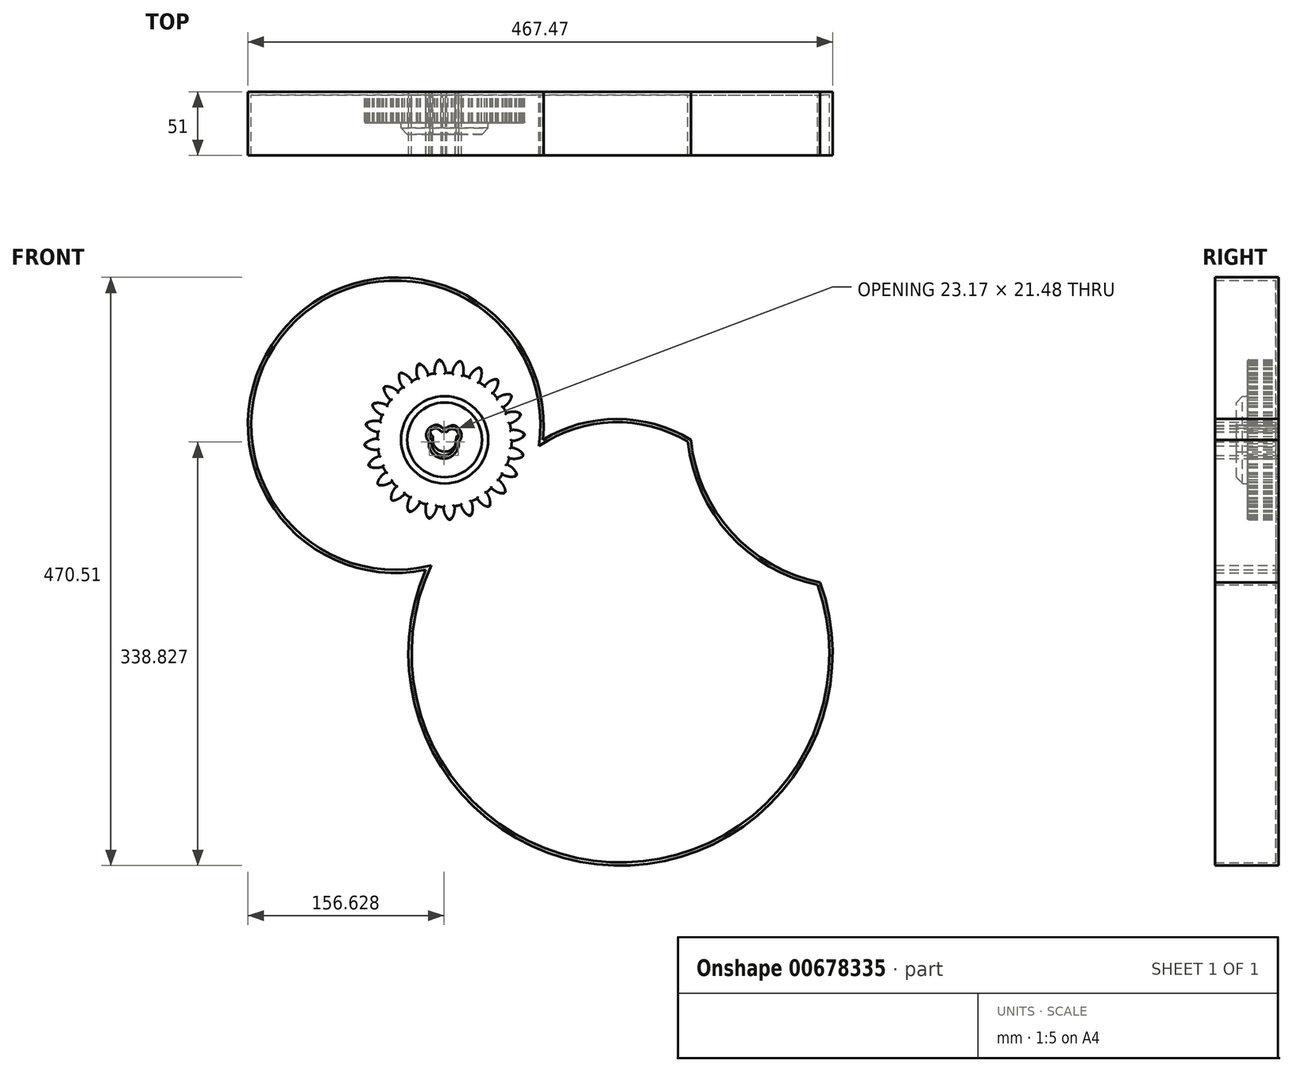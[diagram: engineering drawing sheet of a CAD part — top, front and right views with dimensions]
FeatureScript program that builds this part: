
annotation { "Feature Type Name" : "Feature", "Feature Type Description" : "" }
export const myFeature = defineFeature(function(context is Context, id is Id, definition is map)
    precondition{}
    {
        {
            var Q0;
            Q0=qCreatedBy(makeId("Front.planeOp"),FACE);
            var sketch = newSketch(context, id + "F0", { "sketchPlane" : qUnion([Q0])});
            skCircle(sketch, "E0", {"center": v(0, 0) * mm, "radius": 53.72 * mm});
            skCircle(sketch, "E1", {"center": v(0, 0) * mm, "radius": 58.67 * mm, "construction": true});
            skCircle(sketch, "E2", {"center": v(0, 0) * mm, "radius": 63.5 * mm, "construction": true});
            skLineSegment(sketch, "E3", {"start": v(0, 83.52) * mm, "end": v(0, 0) * mm, "construction": true});
            skLineSegment(sketch, "E4", {"start": v(0, 0) * mm, "end": v(-5.47, 83.52) * mm, "construction": true});
            skLineSegment(sketch, "E5", {"start": v(0, 58.67) * mm, "end": v(-56.46, 38.13) * mm, "construction": true});
            skLineSegment(sketch, "E6", {"start": v(0, 58.67) * mm, "end": v(-59.14, 58.67) * mm, "construction": true});
            skCircle(sketch, "E7", {"center": v(0, 0) * mm, "radius": 55.14 * mm, "construction": true});
            skCircle(sketch, "E8", {"center": v(0, 58.67) * mm, "radius": 14.6 * mm, "construction": true});
            skCircle(sketch, "E9", {"center": v(-13.72, 53.68) * mm, "radius": 14.6 * mm, "construction": true});
            skArc(sketch, "E10", {"start": v(0, 58.67) * mm, "mid": v(-1.18, 61.2) * mm, "end": v(-2.86, 63.44) * mm});
            skArc(sketch, "E11", {"start": v(0.88, 53.71) * mm, "mid": v(0.63, 56.23) * mm, "end": v(0, 58.67) * mm});
            skArc(sketch, "E12.MirrorCS", {"start": v(-7.66, 58.17) * mm, "mid": v(-6.82, 60.84) * mm, "end": v(-5.45, 63.27) * mm});
            skArc(sketch, "E13.MirrorCS", {"start": v(-7.88, 53.14) * mm, "mid": v(-7.97, 55.66) * mm, "end": v(-7.66, 58.17) * mm});
            skArc(sketch, "E14", {"start": v(-2.86, 63.44) * mm, "mid": v(-4.19, 63.92) * mm, "end": v(-5.45, 63.27) * mm});
            skCircle(sketch, "E15", {"center": v(0.01, 0) * mm, "radius": 34.89 * mm});
            skCircle(sketch, "E16", {"center": v(0.01, 0) * mm, "radius": 9.5 * mm});
            skCircle(sketch, "E17", {"center": v(-6.45, 6.97) * mm, "radius": 5.08 * mm});
            skCircle(sketch, "E18", {"center": v(6.77, 6.7) * mm, "radius": 4.94 * mm});
            skSolve(sketch);
        }
        {
            var Q0;
            Q0=makeQuery(id+"F0.imprint","IMPRINT",FACE,{"disambiguationData":[TD([[makeQuery(id+"F0.imprint","IMPRINT",EDGE,{"derivedFrom":sQuery(id+"F0.wireOp",EDGE,"E15")}),-1.0]])]});
            var Q1;
            Q1=makeQuery(id+"F0.imprint","IMPRINT",FACE,{"disambiguationData":[TD([[makeQuery(id+"F0.imprint","IMPRINT",EDGE,{"derivedFrom":sQuery(id+"F0.wireOp",EDGE,"E10")}),1.0]])]});
            extrude(context, id + "F1", {"entities" : qUnion([Q0, Q1]), "depth" : 25 * mm, "offsetDistance" : 25 * mm});
        }
        {
            var Q0;
            Q0=makeQuery(id+"F1.opExtrude","SWEPT_BODY",BODY,{"disambiguationData":[OSD([sQuery(id+"F0.wireOp",EDGE,"E0"),sQuery(id+"F0.wireOp",EDGE,"E10"),sQuery(id+"F0.wireOp",EDGE,"E11"),sQuery(id+"F0.wireOp",EDGE,"E12.MirrorCS"),sQuery(id+"F0.wireOp",EDGE,"E13.MirrorCS"),sQuery(id+"F0.wireOp",EDGE,"E14")])]});
            var Q1;
            Q1=makeQuery(id+"F1.opExtrude","SWEPT_FACE",FACE,{"disambiguationData":[OSD([sQuery(id+"F0.wireOp",EDGE,"E0")])]});
            circularPattern(context, id + "F2", {"entities" : qUnion([Q0]), "axis" : qUnion([Q1]), "angle" : 360 * degree, "instanceCount" : 24, "equalSpace" : true});
        }
        {
            var Q0;
            Q0=makeQuery(id+"F0.imprint","IMPRINT",FACE,{"disambiguationData":[TD([[makeQuery(id+"F0.imprint","IMPRINT",EDGE,{"derivedFrom":sQuery(id+"F0.wireOp",EDGE,"E15")}),1.0]])]});
            extrude(context, id + "F3", {"entities" : qUnion([Q0]), "operationType" : NewBodyOperationType.ADD, "depth" : 33.9 * mm, "offsetDistance" : 25 * mm});
        }
        {
            var Q0;
            Q0=makeQuery(id+"F3.opExtrude","CAP_EDGE",EDGE,{"disambiguationData":[OSD([sQuery(id+"F0.wireOp",EDGE,"E15")])],"isStart":true});
            var Q1;
            Q1=makeQuery(id+"F3.opExtrude","CAP_EDGE",EDGE,{"disambiguationData":[OSD([sQuery(id+"F0.wireOp",EDGE,"E15")])],"isStart":false});
            chamfer(context, id + "F4", {"entities" : qUnion([Q0, Q1]), "width" : 5 * mm, "tangentPropagation" : true});
        }
        {
            var Q0;
            {var subQ0=makeQuery(id+"F1.opExtrude","CAP_FACE",FACE,{"disambiguationData":[OSD([sQuery(id+"F0.wireOp",EDGE,"E0"),sQuery(id+"F0.wireOp",EDGE,"E10"),sQuery(id+"F0.wireOp",EDGE,"E11"),sQuery(id+"F0.wireOp",EDGE,"E12.MirrorCS"),sQuery(id+"F0.wireOp",EDGE,"E13.MirrorCS"),sQuery(id+"F0.wireOp",EDGE,"E14"),sQuery(id+"F0.wireOp",EDGE,"E15")])],"isStart":false});Q0=makeQuery(id+"F3.boolean.opBoolean","MERGE",FACE,{"derivedFrom":[subQ0,makeQuery(id+"F2.opPattern","COPY",FACE,{"derivedFrom":subQ0,"instanceName":"1"}),makeQuery(id+"F2.opPattern","COPY",FACE,{"derivedFrom":subQ0,"instanceName":"2"}),makeQuery(id+"F2.opPattern","COPY",FACE,{"derivedFrom":subQ0,"instanceName":"3"}),makeQuery(id+"F2.opPattern","COPY",FACE,{"derivedFrom":subQ0,"instanceName":"4"}),makeQuery(id+"F2.opPattern","COPY",FACE,{"derivedFrom":subQ0,"instanceName":"5"}),makeQuery(id+"F2.opPattern","COPY",FACE,{"derivedFrom":subQ0,"instanceName":"6"}),makeQuery(id+"F2.opPattern","COPY",FACE,{"derivedFrom":subQ0,"instanceName":"7"}),makeQuery(id+"F2.opPattern","COPY",FACE,{"derivedFrom":subQ0,"instanceName":"8"}),makeQuery(id+"F2.opPattern","COPY",FACE,{"derivedFrom":subQ0,"instanceName":"9"}),makeQuery(id+"F2.opPattern","COPY",FACE,{"derivedFrom":subQ0,"instanceName":"10"}),makeQuery(id+"F2.opPattern","COPY",FACE,{"derivedFrom":subQ0,"instanceName":"11"}),makeQuery(id+"F2.opPattern","COPY",FACE,{"derivedFrom":subQ0,"instanceName":"12"}),makeQuery(id+"F2.opPattern","COPY",FACE,{"derivedFrom":subQ0,"instanceName":"13"}),makeQuery(id+"F2.opPattern","COPY",FACE,{"derivedFrom":subQ0,"instanceName":"14"}),makeQuery(id+"F2.opPattern","COPY",FACE,{"derivedFrom":subQ0,"instanceName":"15"}),makeQuery(id+"F2.opPattern","COPY",FACE,{"derivedFrom":subQ0,"instanceName":"16"}),makeQuery(id+"F2.opPattern","COPY",FACE,{"derivedFrom":subQ0,"instanceName":"17"}),makeQuery(id+"F2.opPattern","COPY",FACE,{"derivedFrom":subQ0,"instanceName":"18"}),makeQuery(id+"F2.opPattern","COPY",FACE,{"derivedFrom":subQ0,"instanceName":"19"}),makeQuery(id+"F2.opPattern","COPY",FACE,{"derivedFrom":subQ0,"instanceName":"20"}),makeQuery(id+"F2.opPattern","COPY",FACE,{"derivedFrom":subQ0,"instanceName":"21"}),makeQuery(id+"F2.opPattern","COPY",FACE,{"derivedFrom":subQ0,"instanceName":"22"}),makeQuery(id+"F2.opPattern","COPY",FACE,{"derivedFrom":subQ0,"instanceName":"23"})]});}
            var Q1;
            {var subQ0=sQuery(id+"F0.wireOp",EDGE,"E15");var subQ1=makeQuery(id+"F1.opExtrude","CAP_FACE",FACE,{"disambiguationData":[OSD([sQuery(id+"F0.wireOp",EDGE,"E0"),sQuery(id+"F0.wireOp",EDGE,"E10"),sQuery(id+"F0.wireOp",EDGE,"E11"),sQuery(id+"F0.wireOp",EDGE,"E12.MirrorCS"),sQuery(id+"F0.wireOp",EDGE,"E13.MirrorCS"),sQuery(id+"F0.wireOp",EDGE,"E14"),subQ0])],"isStart":true});Q1=makeQuery(id+"F3.boolean.opBoolean","MERGE",FACE,{"derivedFrom":[subQ1,makeQuery(id+"F2.opPattern","COPY",FACE,{"derivedFrom":subQ1,"instanceName":"1"}),makeQuery(id+"F2.opPattern","COPY",FACE,{"derivedFrom":subQ1,"instanceName":"2"}),makeQuery(id+"F2.opPattern","COPY",FACE,{"derivedFrom":subQ1,"instanceName":"3"}),makeQuery(id+"F2.opPattern","COPY",FACE,{"derivedFrom":subQ1,"instanceName":"4"}),makeQuery(id+"F2.opPattern","COPY",FACE,{"derivedFrom":subQ1,"instanceName":"5"}),makeQuery(id+"F2.opPattern","COPY",FACE,{"derivedFrom":subQ1,"instanceName":"6"}),makeQuery(id+"F2.opPattern","COPY",FACE,{"derivedFrom":subQ1,"instanceName":"7"}),makeQuery(id+"F2.opPattern","COPY",FACE,{"derivedFrom":subQ1,"instanceName":"8"}),makeQuery(id+"F2.opPattern","COPY",FACE,{"derivedFrom":subQ1,"instanceName":"9"}),makeQuery(id+"F2.opPattern","COPY",FACE,{"derivedFrom":subQ1,"instanceName":"10"}),makeQuery(id+"F2.opPattern","COPY",FACE,{"derivedFrom":subQ1,"instanceName":"11"}),makeQuery(id+"F2.opPattern","COPY",FACE,{"derivedFrom":subQ1,"instanceName":"12"}),makeQuery(id+"F2.opPattern","COPY",FACE,{"derivedFrom":subQ1,"instanceName":"13"}),makeQuery(id+"F2.opPattern","COPY",FACE,{"derivedFrom":subQ1,"instanceName":"14"}),makeQuery(id+"F2.opPattern","COPY",FACE,{"derivedFrom":subQ1,"instanceName":"15"}),makeQuery(id+"F2.opPattern","COPY",FACE,{"derivedFrom":subQ1,"instanceName":"16"}),makeQuery(id+"F2.opPattern","COPY",FACE,{"derivedFrom":subQ1,"instanceName":"17"}),makeQuery(id+"F2.opPattern","COPY",FACE,{"derivedFrom":subQ1,"instanceName":"18"}),makeQuery(id+"F2.opPattern","COPY",FACE,{"derivedFrom":subQ1,"instanceName":"19"}),makeQuery(id+"F2.opPattern","COPY",FACE,{"derivedFrom":subQ1,"instanceName":"20"}),makeQuery(id+"F2.opPattern","COPY",FACE,{"derivedFrom":subQ1,"instanceName":"21"}),makeQuery(id+"F2.opPattern","COPY",FACE,{"derivedFrom":subQ1,"instanceName":"22"}),makeQuery(id+"F2.opPattern","COPY",FACE,{"derivedFrom":subQ1,"instanceName":"23"}),makeQuery(id+"F3.opExtrude","CAP_FACE",FACE,{"disambiguationData":[OSD([subQ0,sQuery(id+"F0.wireOp",EDGE,"E16"),sQuery(id+"F0.wireOp",EDGE,"E17"),sQuery(id+"F0.wireOp",EDGE,"E18")])],"isStart":true})]});}
            var Q2;
            Q2=makeQuery(id+"F3.opExtrude","SWEPT_FACE",FACE,{"disambiguationData":[OSD([sQuery(id+"F0.wireOp",EDGE,"E17")])]});
            var Q3;
            {var subQ0=sQuery(id+"F0.wireOp",EDGE,"E16");Q3=makeQuery(id+"F3.opExtrude","SWEPT_FACE",FACE,{"disambiguationData":[OSD([subQ0]),TDD([makeQuery(id+"F0.imprint","IMPRINT",EDGE,{"disambiguationData":[TD([[makeQuery(id+"F0.imprint","INTERSECT",VERTEX,{"disambiguationData":[OD(1.0)],"derivedFrom":[subQ0,sQuery(id+"F0.wireOp",EDGE,"E18")]}),1.0]])],"derivedFrom":subQ0})])]});}
            var Q4;
            Q4=makeQuery(id+"F3.opExtrude","SWEPT_FACE",FACE,{"disambiguationData":[OSD([sQuery(id+"F0.wireOp",EDGE,"E18")])]});
            var Q5;
            {var subQ0=sQuery(id+"F0.wireOp",EDGE,"E18");var subQ1=sQuery(id+"F0.wireOp",EDGE,"E16");Q5=makeQuery(id+"F3.opExtrude","SWEPT_EDGE",EDGE,{"disambiguationData":[OSD([subQ1,subQ0]),TDD([makeQuery(id+"F0.imprint","INTERSECT",VERTEX,{"disambiguationData":[OD(0.0)],"derivedFrom":[subQ1,subQ0]})])]});}
            fillet(context, id + "F5", {"entities" : qUnion([Q0, Q1, Q2, Q3, Q4, Q5]), "radius" : 1 * mm, "tangentPropagation" : true, "allowEdgeOverflow" : false});
        }
        {
            var Q0;
            Q0=qCreatedBy(makeId("Front.planeOp"),FACE);
            var sketch = newSketch(context, id + "F6", { "sketchPlane" : qUnion([Q0])});
            skCircle(sketch, "E19", {"center": v(-39.03, 11.71) * mm, "radius": 118.2 * mm});
            skCircle(sketch, "E20.MirrorC", {"center": v(325.03, 12.3) * mm, "radius": 128.63 * mm});
            skArc(sketch, "E21", {"start": v(196.99, 0) * mm, "mid": v(137.79, 16.6) * mm, "end": v(78.6, 0) * mm});
            skArc(sketch, "E22", {"start": v(-15.09, -104.04) * mm, "mid": v(135.36, -340.5) * mm, "end": v(300.33, -113.94) * mm});
            skCircle(sketch, "E23", {"center": v(-0.67, -3) * mm, "radius": 9.5 * mm});
            skCircle(sketch, "E24", {"center": v(-7.14, 3.97) * mm, "radius": 5.08 * mm});
            skCircle(sketch, "E25", {"center": v(6.08, 3.7) * mm, "radius": 4.94 * mm});
            skSolve(sketch);
        }
        {
            var Q0;
            {var subQ0=sQuery(id+"F6.wireOp",EDGE,"E21");Q0=makeQuery(id+"F6.imprint","IMPRINT",FACE,{"disambiguationData":[TD([[makeQuery(id+"F6.imprint","IMPRINT",EDGE,{"derivedFrom":subQ0}),1.0]])]});}
            var Q1;
            {var subQ0=sQuery(id+"F6.wireOp",EDGE,"E19");var subQ1=makeQuery(id+"F6.imprint","INTERSECT",VERTEX,{"derivedFrom":[subQ0,sQuery(id+"F6.wireOp",EDGE,"E21")]});Q1=makeQuery(id+"F6.imprint","IMPRINT",FACE,{"disambiguationData":[TD([[makeQuery(id+"F6.imprint","IMPRINT",EDGE,{"disambiguationData":[TD([[subQ1,1.0]])],"derivedFrom":subQ0}),1.0]])]});}
            var Q2;
            {var subQ0=sQuery(id+"F6.wireOp",EDGE,"E20.MirrorC");var subQ1=makeQuery(id+"F6.imprint","INTERSECT",VERTEX,{"derivedFrom":[subQ0,sQuery(id+"F6.wireOp",EDGE,"E21")]});Q2=makeQuery(id+"F6.imprint","IMPRINT",FACE,{"disambiguationData":[TD([[makeQuery(id+"F6.imprint","IMPRINT",EDGE,{"disambiguationData":[TD([[subQ1,1.0]])],"derivedFrom":subQ0}),-1.0]])]});}
            extrude(context, id + "F7", {"entities" : qUnion([Q0, Q1, Q2]), "depth" : 51 * mm, "offsetDistance" : 25 * mm});
        }
        {
            var Q0;
            Q0=makeQuery(id+"F7.opExtrude","CAP_FACE",FACE,{"disambiguationData":[OSD([sQuery(id+"F6.wireOp",EDGE,"E19"),sQuery(id+"F6.wireOp",EDGE,"E20.MirrorC"),sQuery(id+"F6.wireOp",EDGE,"E21"),sQuery(id+"F6.wireOp",EDGE,"E22")])],"isStart":false});
            shell(context, id + "F8", {"entities" : qUnion([Q0]), "thickness" : 2.5 * mm});
        }
    });
